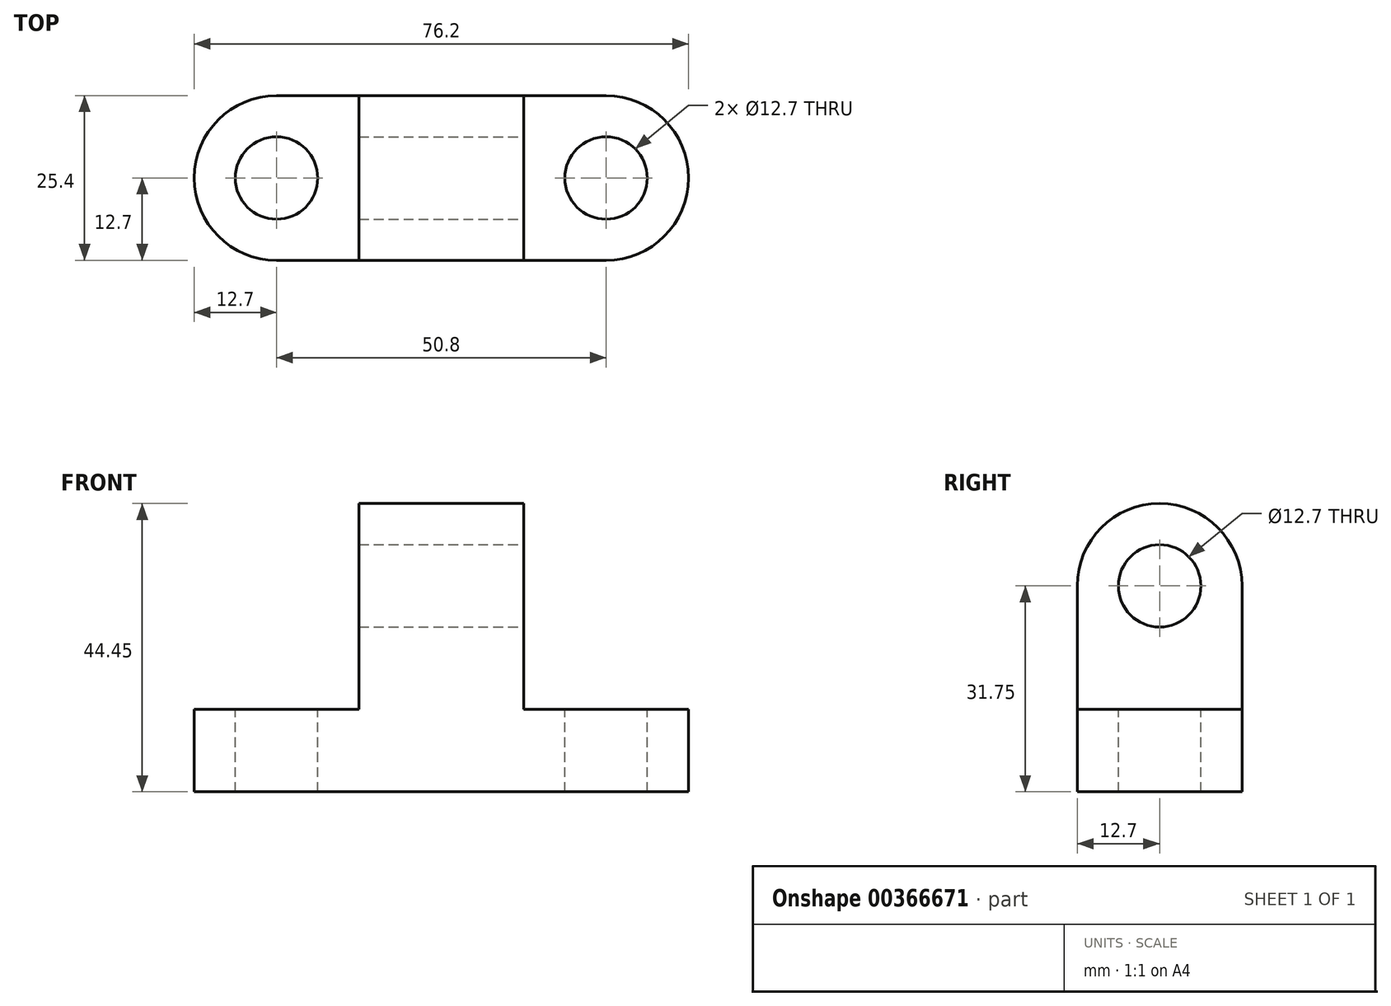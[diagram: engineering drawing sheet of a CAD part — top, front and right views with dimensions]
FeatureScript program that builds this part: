
annotation { "Feature Type Name" : "Feature", "Feature Type Description" : "" }
export const myFeature = defineFeature(function(context is Context, id is Id, definition is map)
    precondition{}
    {
        {
            var Q0;
            Q0=qCreatedBy(makeId("Front.planeOp"),FACE);
            var sketch = newSketch(context, id + "F0", { "sketchPlane" : qUnion([Q0])});
            skLineSegment(sketch, "E0", {"start": v(-76.2, 44.45) * mm, "end": v(0, 44.45) * mm});
            skLineSegment(sketch, "E1", {"start": v(-76.2, 44.45) * mm, "end": v(-76.2, 0) * mm});
            skLineSegment(sketch, "E2", {"start": v(-76.2, 0) * mm, "end": v(0, 0) * mm});
            skLineSegment(sketch, "E3", {"start": v(0, 0) * mm, "end": v(0, 44.45) * mm});
            skSolve(sketch);
        }
        {
            var Q0;
            Q0=makeQuery(id+"F0.imprint","IMPRINT",FACE,{"disambiguationData":[TD([[makeQuery(id+"F0.imprint","IMPRINT",EDGE,{"derivedFrom":sQuery(id+"F0.wireOp",EDGE,"E0")}),-1.0]])]});
            extrude(context, id + "F1", {"entities" : qUnion([Q0]), "depth" : 25.4 * mm});
        }
        {
            var Q0;
            Q0=makeQuery(id+"F1.opExtrude","CAP_FACE",FACE,{"disambiguationData":[OSD([sQuery(id+"F0.wireOp",EDGE,"E0"),sQuery(id+"F0.wireOp",EDGE,"E1"),sQuery(id+"F0.wireOp",EDGE,"E2"),sQuery(id+"F0.wireOp",EDGE,"E3")])],"isStart":false});
            var sketch = newSketch(context, id + "F2", { "sketchPlane" : qUnion([Q0])});
            skLineSegment(sketch, "E4", {"start": v(0, 12.7) * mm, "end": v(-25.4, 12.7) * mm});
            skLineSegment(sketch, "E5", {"start": v(-25.4, 12.7) * mm, "end": v(-25.4, 44.45) * mm});
            skLineSegment(sketch, "E6", {"start": v(-50.8, 44.45) * mm, "end": v(-50.8, 12.7) * mm});
            skLineSegment(sketch, "E7", {"start": v(-50.8, 12.7) * mm, "end": v(-76.2, 12.7) * mm});
            skSolve(sketch);
        }
        {
            var Q0;
            {var subQ0=sQuery(id+"F2.wireOp",EDGE,"E6");Q0=makeQuery(id+"F2.imprint","IMPRINT",FACE,{"disambiguationData":[TD([[makeQuery(id+"F2.imprint","IMPRINT",EDGE,{"derivedFrom":subQ0}),-1.0]])]});}
            var Q1;
            {var subQ0=sQuery(id+"F2.wireOp",EDGE,"E4");Q1=makeQuery(id+"F2.imprint","IMPRINT",FACE,{"disambiguationData":[TD([[makeQuery(id+"F2.imprint","IMPRINT",EDGE,{"derivedFrom":subQ0}),-1.0]])]});}
            extrude(context, id + "F3", {"entities" : qUnion([Q0, Q1]), "operationType" : NewBodyOperationType.REMOVE, "oppositeDirection" : true, "depth" : 25.4 * mm});
        }
        {
            var Q0;
            Q0=makeQuery(id+"F3.boolean.opBoolean","COPY",FACE,{"derivedFrom":makeQuery(id+"F3.opExtrude","SWEPT_FACE",FACE,{"disambiguationData":[OSD([sQuery(id+"F2.wireOp",EDGE,"E5")])]})});
            var sketch = newSketch(context, id + "F4", { "sketchPlane" : qUnion([Q0])});
            skCircle(sketch, "E8", {"center": v(-12.7, 31.75) * mm, "radius": 6.35 * mm});
            skArc(sketch, "E9", {"start": v(0, 31.75) * mm, "mid": v(-12.7, 44.45) * mm, "end": v(-25.4, 31.75) * mm});
            skSolve(sketch);
        }
        {
            var Q0;
            {var subQ0=sQuery(id+"F4.wireOp",EDGE,"E9");var subQ1=sQuery(id+"F2.wireOp",EDGE,"E5");var subQ2=makeQuery(id+"F3.boolean.opBoolean","COPY",EDGE,{"derivedFrom":makeQuery(id+"F3.opExtrude","CAP_EDGE",EDGE,{"disambiguationData":[OSD([subQ1])],"isStart":true})});var subQ3=makeQuery(id+"F4.imprint","INTERSECT",VERTEX,{"derivedFrom":[subQ2,subQ0]});Q0=makeQuery(id+"F4.imprint","IMPRINT",FACE,{"disambiguationData":[TD([[makeQuery(id+"F4.imprint","IMPRINT",EDGE,{"disambiguationData":[TD([[subQ3,1.0]])],"derivedFrom":subQ0}),-1.0]])]});}
            var Q1;
            {var subQ0=sQuery(id+"F4.wireOp",EDGE,"E9");var subQ1=sQuery(id+"F2.wireOp",EDGE,"E5");var subQ2=makeQuery(id+"F3.boolean.opBoolean","COPY",EDGE,{"derivedFrom":makeQuery(id+"F3.opExtrude","CAP_EDGE",EDGE,{"disambiguationData":[OSD([subQ1])],"isStart":false})});var subQ3=makeQuery(id+"F4.imprint","INTERSECT",VERTEX,{"derivedFrom":[subQ2,subQ0]});Q1=makeQuery(id+"F4.imprint","IMPRINT",FACE,{"disambiguationData":[TD([[makeQuery(id+"F4.imprint","IMPRINT",EDGE,{"disambiguationData":[TD([[subQ3,-1.0]])],"derivedFrom":subQ0}),-1.0]])]});}
            var Q2;
            Q2=makeQuery(id+"F4.imprint","IMPRINT",FACE,{"disambiguationData":[TD([[makeQuery(id+"F4.imprint","IMPRINT",EDGE,{"derivedFrom":sQuery(id+"F4.wireOp",EDGE,"E8")}),1.0]])]});
            extrude(context, id + "F5", {"entities" : qUnion([Q0, Q1, Q2]), "operationType" : NewBodyOperationType.REMOVE, "oppositeDirection" : true, "depth" : 25.4 * mm});
        }
        {
            var Q0;
            Q0=makeQuery(id+"F3.boolean.opBoolean","COPY",FACE,{"derivedFrom":makeQuery(id+"F3.opExtrude","SWEPT_FACE",FACE,{"disambiguationData":[OSD([sQuery(id+"F2.wireOp",EDGE,"E4")])]})});
            var sketch = newSketch(context, id + "F6", { "sketchPlane" : qUnion([Q0])});
            skCircle(sketch, "E10", {"center": v(-12.7, -12.7) * mm, "radius": 6.35 * mm});
            skArc(sketch, "E11", {"start": v(-12.7, -25.4) * mm, "mid": v(0, -12.7) * mm, "end": v(-12.7, 0) * mm});
            skSolve(sketch);
        }
        {
            var Q0;
            {var subQ0=sQuery(id+"F6.wireOp",EDGE,"E11");var subQ1=sQuery(id+"F2.wireOp",EDGE,"E4");var subQ2=makeQuery(id+"F3.boolean.opBoolean","COPY",EDGE,{"derivedFrom":makeQuery(id+"F3.opExtrude","CAP_EDGE",EDGE,{"disambiguationData":[OSD([subQ1])],"isStart":true})});var subQ3=makeQuery(id+"F6.imprint","INTERSECT",VERTEX,{"derivedFrom":[subQ2,subQ0]});Q0=makeQuery(id+"F6.imprint","IMPRINT",FACE,{"disambiguationData":[TD([[makeQuery(id+"F6.imprint","IMPRINT",EDGE,{"disambiguationData":[TD([[subQ3,-1.0]])],"derivedFrom":subQ0}),-1.0]])]});}
            var Q1;
            {var subQ0=sQuery(id+"F6.wireOp",EDGE,"E11");var subQ1=sQuery(id+"F2.wireOp",EDGE,"E4");var subQ2=makeQuery(id+"F3.boolean.opBoolean","COPY",EDGE,{"derivedFrom":makeQuery(id+"F3.opExtrude","CAP_EDGE",EDGE,{"disambiguationData":[OSD([subQ1])],"isStart":false})});var subQ3=makeQuery(id+"F6.imprint","INTERSECT",VERTEX,{"derivedFrom":[subQ2,subQ0]});Q1=makeQuery(id+"F6.imprint","IMPRINT",FACE,{"disambiguationData":[TD([[makeQuery(id+"F6.imprint","IMPRINT",EDGE,{"disambiguationData":[TD([[subQ3,1.0]])],"derivedFrom":subQ0}),-1.0]])]});}
            var Q2;
            Q2=makeQuery(id+"F6.imprint","IMPRINT",FACE,{"disambiguationData":[TD([[makeQuery(id+"F6.imprint","IMPRINT",EDGE,{"derivedFrom":sQuery(id+"F6.wireOp",EDGE,"E10")}),1.0]])]});
            extrude(context, id + "F7", {"entities" : qUnion([Q0, Q1, Q2]), "operationType" : NewBodyOperationType.REMOVE, "oppositeDirection" : true, "depth" : 25.4 * mm});
        }
        {
            var Q0;
            Q0=makeQuery(id+"F3.boolean.opBoolean","COPY",FACE,{"derivedFrom":makeQuery(id+"F3.opExtrude","SWEPT_FACE",FACE,{"disambiguationData":[OSD([sQuery(id+"F2.wireOp",EDGE,"E7")])]})});
            var sketch = newSketch(context, id + "F8", { "sketchPlane" : qUnion([Q0])});
            skCircle(sketch, "E12", {"center": v(-63.5, -12.7) * mm, "radius": 6.35 * mm});
            skArc(sketch, "E13", {"start": v(-63.5, 0) * mm, "mid": v(-76.2, -12.7) * mm, "end": v(-63.5, -25.4) * mm});
            skSolve(sketch);
        }
        {
            var Q0;
            {var subQ0=sQuery(id+"F8.wireOp",EDGE,"E13");var subQ1=sQuery(id+"F2.wireOp",EDGE,"E7");var subQ2=makeQuery(id+"F3.boolean.opBoolean","COPY",EDGE,{"derivedFrom":makeQuery(id+"F3.opExtrude","CAP_EDGE",EDGE,{"disambiguationData":[OSD([subQ1])],"isStart":false})});var subQ3=makeQuery(id+"F8.imprint","INTERSECT",VERTEX,{"derivedFrom":[subQ2,subQ0]});Q0=makeQuery(id+"F8.imprint","IMPRINT",FACE,{"disambiguationData":[TD([[makeQuery(id+"F8.imprint","IMPRINT",EDGE,{"disambiguationData":[TD([[subQ3,-1.0]])],"derivedFrom":subQ0}),-1.0]])]});}
            var Q1;
            {var subQ0=sQuery(id+"F8.wireOp",EDGE,"E13");var subQ1=sQuery(id+"F2.wireOp",EDGE,"E7");var subQ2=makeQuery(id+"F3.boolean.opBoolean","COPY",EDGE,{"derivedFrom":makeQuery(id+"F3.opExtrude","CAP_EDGE",EDGE,{"disambiguationData":[OSD([subQ1])],"isStart":true})});var subQ3=makeQuery(id+"F8.imprint","INTERSECT",VERTEX,{"derivedFrom":[subQ2,subQ0]});Q1=makeQuery(id+"F8.imprint","IMPRINT",FACE,{"disambiguationData":[TD([[makeQuery(id+"F8.imprint","IMPRINT",EDGE,{"disambiguationData":[TD([[subQ3,1.0]])],"derivedFrom":subQ0}),-1.0]])]});}
            var Q2;
            Q2=makeQuery(id+"F8.imprint","IMPRINT",FACE,{"disambiguationData":[TD([[makeQuery(id+"F8.imprint","IMPRINT",EDGE,{"derivedFrom":sQuery(id+"F8.wireOp",EDGE,"E12")}),1.0]])]});
            extrude(context, id + "F9", {"entities" : qUnion([Q0, Q1, Q2]), "operationType" : NewBodyOperationType.REMOVE, "oppositeDirection" : true, "depth" : 25.4 * mm});
        }
    });
